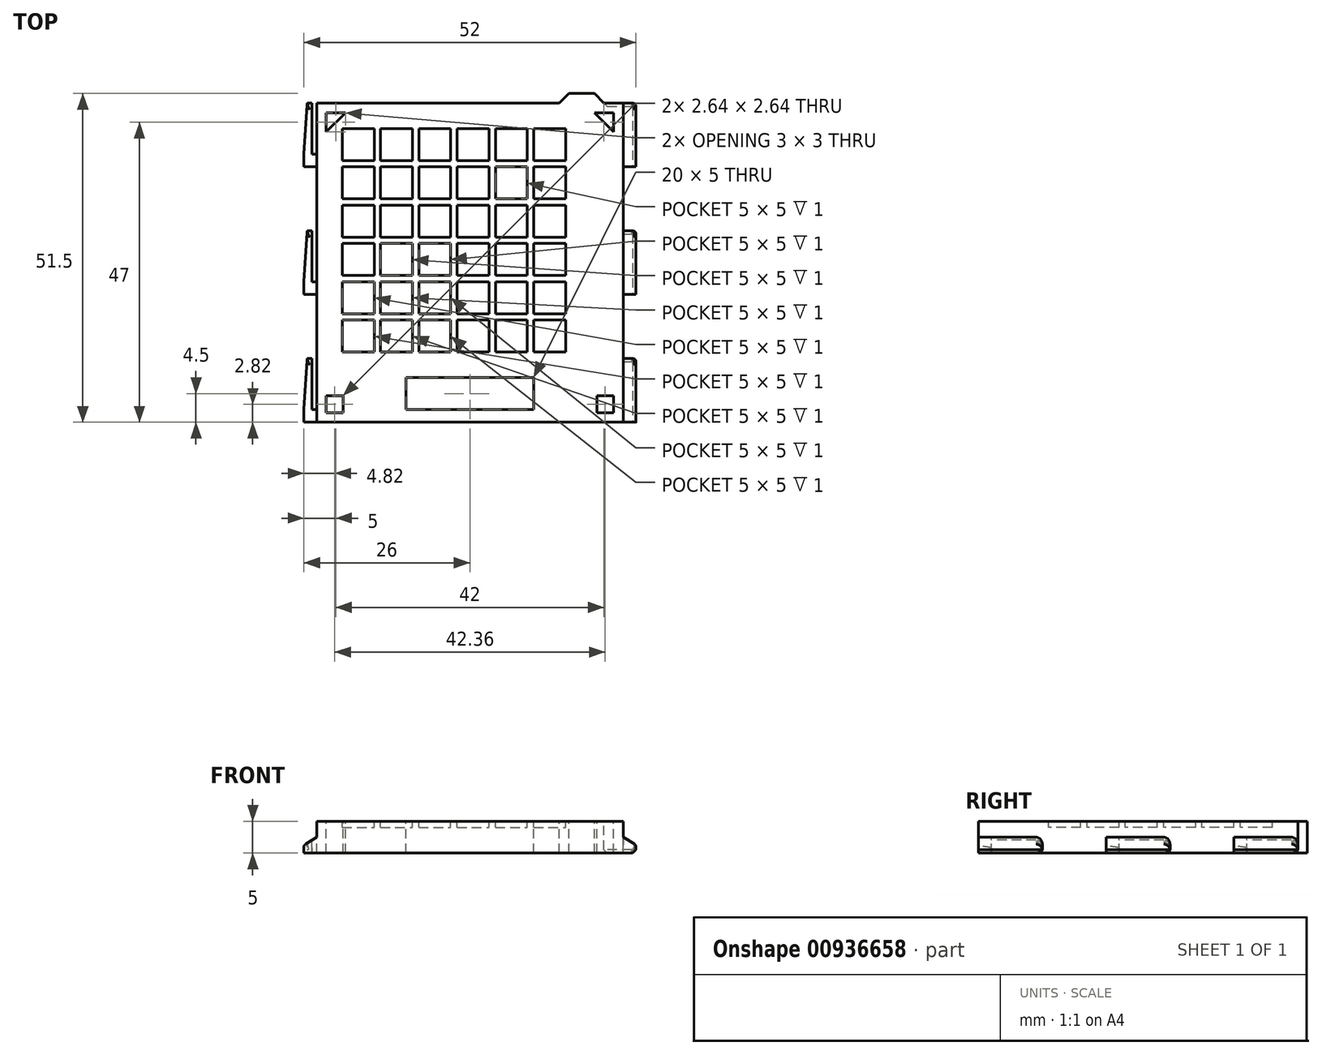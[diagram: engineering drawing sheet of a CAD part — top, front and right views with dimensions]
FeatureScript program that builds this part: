
annotation { "Feature Type Name" : "Feature", "Feature Type Description" : "" }
export const myFeature = defineFeature(function(context is Context, id is Id, definition is map)
    precondition{}
    {
        {
            var Q0;
            Q0=qCreatedBy(makeId("Top.planeOp"),FACE);
            var sketch = newSketch(context, id + "F0", { "sketchPlane" : qUnion([Q0])});
            skLineSegment(sketch, "E0.bottom", {"start": v(0, 0) * mm, "end": v(48, 0) * mm});
            skLineSegment(sketch, "E0.top", {"start": v(0, -50) * mm, "end": v(48, -50) * mm});
            skLineSegment(sketch, "E0.left", {"start": v(0, 0) * mm, "end": v(0, -50) * mm});
            skLineSegment(sketch, "E0.right", {"start": v(48, 0) * mm, "end": v(48, -50) * mm});
            skSolve(sketch);
        }
        {
            var Q0;
            Q0=makeQuery(id+"F0.imprint","IMPRINT",FACE,{"disambiguationData":[TD([[makeQuery(id+"F0.imprint","IMPRINT",EDGE,{"derivedFrom":sQuery(id+"F0.wireOp",EDGE,"E0.bottom")}),-1.0]])]});
            extrude(context, id + "F1", {"entities" : qUnion([Q0]), "depth" : 5 * mm, "offsetDistance" : 25 * mm});
        }
        {
            var Q0;
            Q0=makeQuery(id+"F1.opExtrude","CAP_FACE",FACE,{"disambiguationData":[OSD([sQuery(id+"F0.wireOp",EDGE,"E0.bottom"),sQuery(id+"F0.wireOp",EDGE,"E0.top"),sQuery(id+"F0.wireOp",EDGE,"E0.left"),sQuery(id+"F0.wireOp",EDGE,"E0.right")])],"isStart":false});
            var sketch = newSketch(context, id + "F2", { "sketchPlane" : qUnion([Q0])});
            skLineSegment(sketch, "E1.bottom", {"start": v(4, -4) * mm, "end": v(9, -4) * mm});
            skLineSegment(sketch, "E1.top", {"start": v(4, -9) * mm, "end": v(9, -9) * mm});
            skLineSegment(sketch, "E1.left", {"start": v(4, -4) * mm, "end": v(4, -9) * mm});
            skLineSegment(sketch, "E1.right", {"start": v(9, -4) * mm, "end": v(9, -9) * mm});
            skLineSegment(sketch, "E2.0.1.0", {"start": v(4, -15) * mm, "end": v(9, -15) * mm});
            skLineSegment(sketch, "E2.0.1.1", {"start": v(9, -10) * mm, "end": v(9, -15) * mm});
            skLineSegment(sketch, "E2.0.1.2", {"start": v(4, -10) * mm, "end": v(4, -15) * mm});
            skLineSegment(sketch, "E2.0.1.3", {"start": v(4, -10) * mm, "end": v(9, -10) * mm});
            skLineSegment(sketch, "E2.0.2.0", {"start": v(4, -21) * mm, "end": v(9, -21) * mm});
            skLineSegment(sketch, "E2.0.2.1", {"start": v(9, -16) * mm, "end": v(9, -21) * mm});
            skLineSegment(sketch, "E2.0.2.2", {"start": v(4, -16) * mm, "end": v(4, -21) * mm});
            skLineSegment(sketch, "E2.0.2.3", {"start": v(4, -16) * mm, "end": v(9, -16) * mm});
            skLineSegment(sketch, "E2.0.3.0", {"start": v(4, -27) * mm, "end": v(9, -27) * mm});
            skLineSegment(sketch, "E2.0.3.1", {"start": v(9, -22) * mm, "end": v(9, -27) * mm});
            skLineSegment(sketch, "E2.0.3.2", {"start": v(4, -22) * mm, "end": v(4, -27) * mm});
            skLineSegment(sketch, "E2.0.3.3", {"start": v(4, -22) * mm, "end": v(9, -22) * mm});
            skLineSegment(sketch, "E2.0.4.0", {"start": v(4, -33) * mm, "end": v(9, -33) * mm});
            skLineSegment(sketch, "E2.0.4.1", {"start": v(9, -28) * mm, "end": v(9, -33) * mm});
            skLineSegment(sketch, "E2.0.4.2", {"start": v(4, -28) * mm, "end": v(4, -33) * mm});
            skLineSegment(sketch, "E2.0.4.3", {"start": v(4, -28) * mm, "end": v(9, -28) * mm});
            skLineSegment(sketch, "E2.0.5.0", {"start": v(4, -39) * mm, "end": v(9, -39) * mm});
            skLineSegment(sketch, "E2.0.5.1", {"start": v(9, -34) * mm, "end": v(9, -39) * mm});
            skLineSegment(sketch, "E2.0.5.2", {"start": v(4, -34) * mm, "end": v(4, -39) * mm});
            skLineSegment(sketch, "E2.0.5.3", {"start": v(4, -34) * mm, "end": v(9, -34) * mm});
            skLineSegment(sketch, "E2.1.0.0", {"start": v(10, -9) * mm, "end": v(15, -9) * mm});
            skLineSegment(sketch, "E2.1.0.1", {"start": v(15, -4) * mm, "end": v(15, -9) * mm});
            skLineSegment(sketch, "E2.1.0.2", {"start": v(10, -4) * mm, "end": v(10, -9) * mm});
            skLineSegment(sketch, "E2.1.0.3", {"start": v(10, -4) * mm, "end": v(15, -4) * mm});
            skLineSegment(sketch, "E2.1.1.0", {"start": v(10, -15) * mm, "end": v(15, -15) * mm});
            skLineSegment(sketch, "E2.1.1.1", {"start": v(15, -10) * mm, "end": v(15, -15) * mm});
            skLineSegment(sketch, "E2.1.1.2", {"start": v(10, -10) * mm, "end": v(10, -15) * mm});
            skLineSegment(sketch, "E2.1.1.3", {"start": v(10, -10) * mm, "end": v(15, -10) * mm});
            skLineSegment(sketch, "E2.1.2.0", {"start": v(10, -21) * mm, "end": v(15, -21) * mm});
            skLineSegment(sketch, "E2.1.2.1", {"start": v(15, -16) * mm, "end": v(15, -21) * mm});
            skLineSegment(sketch, "E2.1.2.2", {"start": v(10, -16) * mm, "end": v(10, -21) * mm});
            skLineSegment(sketch, "E2.1.2.3", {"start": v(10, -16) * mm, "end": v(15, -16) * mm});
            skLineSegment(sketch, "E2.1.3.0", {"start": v(10, -27) * mm, "end": v(15, -27) * mm});
            skLineSegment(sketch, "E2.1.3.1", {"start": v(15, -22) * mm, "end": v(15, -27) * mm});
            skLineSegment(sketch, "E2.1.3.2", {"start": v(10, -22) * mm, "end": v(10, -27) * mm});
            skLineSegment(sketch, "E2.1.3.3", {"start": v(10, -22) * mm, "end": v(15, -22) * mm});
            skLineSegment(sketch, "E2.1.4.0", {"start": v(10, -33) * mm, "end": v(15, -33) * mm});
            skLineSegment(sketch, "E2.1.4.1", {"start": v(15, -28) * mm, "end": v(15, -33) * mm});
            skLineSegment(sketch, "E2.1.4.2", {"start": v(10, -28) * mm, "end": v(10, -33) * mm});
            skLineSegment(sketch, "E2.1.4.3", {"start": v(10, -28) * mm, "end": v(15, -28) * mm});
            skLineSegment(sketch, "E2.1.5.0", {"start": v(10, -39) * mm, "end": v(15, -39) * mm});
            skLineSegment(sketch, "E2.1.5.1", {"start": v(15, -34) * mm, "end": v(15, -39) * mm});
            skLineSegment(sketch, "E2.1.5.2", {"start": v(10, -34) * mm, "end": v(10, -39) * mm});
            skLineSegment(sketch, "E2.1.5.3", {"start": v(10, -34) * mm, "end": v(15, -34) * mm});
            skLineSegment(sketch, "E2.2.0.0", {"start": v(16, -9) * mm, "end": v(21, -9) * mm});
            skLineSegment(sketch, "E2.2.0.1", {"start": v(21, -4) * mm, "end": v(21, -9) * mm});
            skLineSegment(sketch, "E2.2.0.2", {"start": v(16, -4) * mm, "end": v(16, -9) * mm});
            skLineSegment(sketch, "E2.2.0.3", {"start": v(16, -4) * mm, "end": v(21, -4) * mm});
            skLineSegment(sketch, "E2.2.1.0", {"start": v(16, -15) * mm, "end": v(21, -15) * mm});
            skLineSegment(sketch, "E2.2.1.1", {"start": v(21, -10) * mm, "end": v(21, -15) * mm});
            skLineSegment(sketch, "E2.2.1.2", {"start": v(16, -10) * mm, "end": v(16, -15) * mm});
            skLineSegment(sketch, "E2.2.1.3", {"start": v(16, -10) * mm, "end": v(21, -10) * mm});
            skLineSegment(sketch, "E2.2.2.0", {"start": v(16, -21) * mm, "end": v(21, -21) * mm});
            skLineSegment(sketch, "E2.2.2.1", {"start": v(21, -16) * mm, "end": v(21, -21) * mm});
            skLineSegment(sketch, "E2.2.2.2", {"start": v(16, -16) * mm, "end": v(16, -21) * mm});
            skLineSegment(sketch, "E2.2.2.3", {"start": v(16, -16) * mm, "end": v(21, -16) * mm});
            skLineSegment(sketch, "E2.2.3.0", {"start": v(16, -27) * mm, "end": v(21, -27) * mm});
            skLineSegment(sketch, "E2.2.3.1", {"start": v(21, -22) * mm, "end": v(21, -27) * mm});
            skLineSegment(sketch, "E2.2.3.2", {"start": v(16, -22) * mm, "end": v(16, -27) * mm});
            skLineSegment(sketch, "E2.2.3.3", {"start": v(16, -22) * mm, "end": v(21, -22) * mm});
            skLineSegment(sketch, "E2.2.4.0", {"start": v(16, -33) * mm, "end": v(21, -33) * mm});
            skLineSegment(sketch, "E2.2.4.1", {"start": v(21, -28) * mm, "end": v(21, -33) * mm});
            skLineSegment(sketch, "E2.2.4.2", {"start": v(16, -28) * mm, "end": v(16, -33) * mm});
            skLineSegment(sketch, "E2.2.4.3", {"start": v(16, -28) * mm, "end": v(21, -28) * mm});
            skLineSegment(sketch, "E2.2.5.0", {"start": v(16, -39) * mm, "end": v(21, -39) * mm});
            skLineSegment(sketch, "E2.2.5.1", {"start": v(21, -34) * mm, "end": v(21, -39) * mm});
            skLineSegment(sketch, "E2.2.5.2", {"start": v(16, -34) * mm, "end": v(16, -39) * mm});
            skLineSegment(sketch, "E2.2.5.3", {"start": v(16, -34) * mm, "end": v(21, -34) * mm});
            skLineSegment(sketch, "E2.3.0.0", {"start": v(22, -9) * mm, "end": v(27, -9) * mm});
            skLineSegment(sketch, "E2.3.0.1", {"start": v(27, -4) * mm, "end": v(27, -9) * mm});
            skLineSegment(sketch, "E2.3.0.2", {"start": v(22, -4) * mm, "end": v(22, -9) * mm});
            skLineSegment(sketch, "E2.3.0.3", {"start": v(22, -4) * mm, "end": v(27, -4) * mm});
            skLineSegment(sketch, "E2.3.1.0", {"start": v(22, -15) * mm, "end": v(27, -15) * mm});
            skLineSegment(sketch, "E2.3.1.1", {"start": v(27, -10) * mm, "end": v(27, -15) * mm});
            skLineSegment(sketch, "E2.3.1.2", {"start": v(22, -10) * mm, "end": v(22, -15) * mm});
            skLineSegment(sketch, "E2.3.1.3", {"start": v(22, -10) * mm, "end": v(27, -10) * mm});
            skLineSegment(sketch, "E2.3.2.0", {"start": v(22, -21) * mm, "end": v(27, -21) * mm});
            skLineSegment(sketch, "E2.3.2.1", {"start": v(27, -16) * mm, "end": v(27, -21) * mm});
            skLineSegment(sketch, "E2.3.2.2", {"start": v(22, -16) * mm, "end": v(22, -21) * mm});
            skLineSegment(sketch, "E2.3.2.3", {"start": v(22, -16) * mm, "end": v(27, -16) * mm});
            skLineSegment(sketch, "E2.3.3.0", {"start": v(22, -27) * mm, "end": v(27, -27) * mm});
            skLineSegment(sketch, "E2.3.3.1", {"start": v(27, -22) * mm, "end": v(27, -27) * mm});
            skLineSegment(sketch, "E2.3.3.2", {"start": v(22, -22) * mm, "end": v(22, -27) * mm});
            skLineSegment(sketch, "E2.3.3.3", {"start": v(22, -22) * mm, "end": v(27, -22) * mm});
            skLineSegment(sketch, "E2.3.4.0", {"start": v(22, -33) * mm, "end": v(27, -33) * mm});
            skLineSegment(sketch, "E2.3.4.1", {"start": v(27, -28) * mm, "end": v(27, -33) * mm});
            skLineSegment(sketch, "E2.3.4.2", {"start": v(22, -28) * mm, "end": v(22, -33) * mm});
            skLineSegment(sketch, "E2.3.4.3", {"start": v(22, -28) * mm, "end": v(27, -28) * mm});
            skLineSegment(sketch, "E2.3.5.0", {"start": v(22, -39) * mm, "end": v(27, -39) * mm});
            skLineSegment(sketch, "E2.3.5.1", {"start": v(27, -34) * mm, "end": v(27, -39) * mm});
            skLineSegment(sketch, "E2.3.5.2", {"start": v(22, -34) * mm, "end": v(22, -39) * mm});
            skLineSegment(sketch, "E2.3.5.3", {"start": v(22, -34) * mm, "end": v(27, -34) * mm});
            skLineSegment(sketch, "E2.4.0.0", {"start": v(28, -9) * mm, "end": v(33, -9) * mm});
            skLineSegment(sketch, "E2.4.0.1", {"start": v(33, -4) * mm, "end": v(33, -9) * mm});
            skLineSegment(sketch, "E2.4.0.2", {"start": v(28, -4) * mm, "end": v(28, -9) * mm});
            skLineSegment(sketch, "E2.4.0.3", {"start": v(28, -4) * mm, "end": v(33, -4) * mm});
            skLineSegment(sketch, "E2.4.1.0", {"start": v(28, -15) * mm, "end": v(33, -15) * mm});
            skLineSegment(sketch, "E2.4.1.1", {"start": v(33, -10) * mm, "end": v(33, -15) * mm});
            skLineSegment(sketch, "E2.4.1.2", {"start": v(28, -10) * mm, "end": v(28, -15) * mm});
            skLineSegment(sketch, "E2.4.1.3", {"start": v(28, -10) * mm, "end": v(33, -10) * mm});
            skLineSegment(sketch, "E2.4.2.0", {"start": v(28, -21) * mm, "end": v(33, -21) * mm});
            skLineSegment(sketch, "E2.4.2.1", {"start": v(33, -16) * mm, "end": v(33, -21) * mm});
            skLineSegment(sketch, "E2.4.2.2", {"start": v(28, -16) * mm, "end": v(28, -21) * mm});
            skLineSegment(sketch, "E2.4.2.3", {"start": v(28, -16) * mm, "end": v(33, -16) * mm});
            skLineSegment(sketch, "E2.4.3.0", {"start": v(28, -27) * mm, "end": v(33, -27) * mm});
            skLineSegment(sketch, "E2.4.3.1", {"start": v(33, -22) * mm, "end": v(33, -27) * mm});
            skLineSegment(sketch, "E2.4.3.2", {"start": v(28, -22) * mm, "end": v(28, -27) * mm});
            skLineSegment(sketch, "E2.4.3.3", {"start": v(28, -22) * mm, "end": v(33, -22) * mm});
            skLineSegment(sketch, "E2.4.4.0", {"start": v(28, -33) * mm, "end": v(33, -33) * mm});
            skLineSegment(sketch, "E2.4.4.1", {"start": v(33, -28) * mm, "end": v(33, -33) * mm});
            skLineSegment(sketch, "E2.4.4.2", {"start": v(28, -28) * mm, "end": v(28, -33) * mm});
            skLineSegment(sketch, "E2.4.4.3", {"start": v(28, -28) * mm, "end": v(33, -28) * mm});
            skLineSegment(sketch, "E2.4.5.0", {"start": v(28, -39) * mm, "end": v(33, -39) * mm});
            skLineSegment(sketch, "E2.4.5.1", {"start": v(33, -34) * mm, "end": v(33, -39) * mm});
            skLineSegment(sketch, "E2.4.5.2", {"start": v(28, -34) * mm, "end": v(28, -39) * mm});
            skLineSegment(sketch, "E2.4.5.3", {"start": v(28, -34) * mm, "end": v(33, -34) * mm});
            skLineSegment(sketch, "E2.5.0.0", {"start": v(34, -9) * mm, "end": v(39, -9) * mm});
            skLineSegment(sketch, "E2.5.0.1", {"start": v(39, -4) * mm, "end": v(39, -9) * mm});
            skLineSegment(sketch, "E2.5.0.2", {"start": v(34, -4) * mm, "end": v(34, -9) * mm});
            skLineSegment(sketch, "E2.5.0.3", {"start": v(34, -4) * mm, "end": v(39, -4) * mm});
            skLineSegment(sketch, "E2.5.1.0", {"start": v(34, -15) * mm, "end": v(39, -15) * mm});
            skLineSegment(sketch, "E2.5.1.1", {"start": v(39, -10) * mm, "end": v(39, -15) * mm});
            skLineSegment(sketch, "E2.5.1.2", {"start": v(34, -10) * mm, "end": v(34, -15) * mm});
            skLineSegment(sketch, "E2.5.1.3", {"start": v(34, -10) * mm, "end": v(39, -10) * mm});
            skLineSegment(sketch, "E2.5.2.0", {"start": v(34, -21) * mm, "end": v(39, -21) * mm});
            skLineSegment(sketch, "E2.5.2.1", {"start": v(39, -16) * mm, "end": v(39, -21) * mm});
            skLineSegment(sketch, "E2.5.2.2", {"start": v(34, -16) * mm, "end": v(34, -21) * mm});
            skLineSegment(sketch, "E2.5.2.3", {"start": v(34, -16) * mm, "end": v(39, -16) * mm});
            skLineSegment(sketch, "E2.5.3.0", {"start": v(34, -27) * mm, "end": v(39, -27) * mm});
            skLineSegment(sketch, "E2.5.3.1", {"start": v(39, -22) * mm, "end": v(39, -27) * mm});
            skLineSegment(sketch, "E2.5.3.2", {"start": v(34, -22) * mm, "end": v(34, -27) * mm});
            skLineSegment(sketch, "E2.5.3.3", {"start": v(34, -22) * mm, "end": v(39, -22) * mm});
            skLineSegment(sketch, "E2.5.4.0", {"start": v(34, -33) * mm, "end": v(39, -33) * mm});
            skLineSegment(sketch, "E2.5.4.1", {"start": v(39, -28) * mm, "end": v(39, -33) * mm});
            skLineSegment(sketch, "E2.5.4.2", {"start": v(34, -28) * mm, "end": v(34, -33) * mm});
            skLineSegment(sketch, "E2.5.4.3", {"start": v(34, -28) * mm, "end": v(39, -28) * mm});
            skLineSegment(sketch, "E2.5.5.0", {"start": v(34, -39) * mm, "end": v(39, -39) * mm});
            skLineSegment(sketch, "E2.5.5.1", {"start": v(39, -34) * mm, "end": v(39, -39) * mm});
            skLineSegment(sketch, "E2.5.5.2", {"start": v(34, -34) * mm, "end": v(34, -39) * mm});
            skLineSegment(sketch, "E2.5.5.3", {"start": v(34, -34) * mm, "end": v(39, -34) * mm});
            skLineSegment(sketch, "E2.direction1", {"start": v(4, -9) * mm, "end": v(10, -9) * mm, "construction": true});
            skLineSegment(sketch, "E2.direction2", {"start": v(4, -9) * mm, "end": v(4, -15) * mm, "construction": true});
            skSolve(sketch);
        }
        {
            var Q0;
            Q0=makeQuery(id+"F2.imprint","IMPRINT",FACE,{"disambiguationData":[TD([[makeQuery(id+"F2.imprint","IMPRINT",EDGE,{"derivedFrom":sQuery(id+"F2.wireOp",EDGE,"E1.bottom")}),-1.0]])]});
            var Q1;
            Q1=makeQuery(id+"F2.imprint","IMPRINT",FACE,{"disambiguationData":[TD([[makeQuery(id+"F2.imprint","IMPRINT",EDGE,{"derivedFrom":sQuery(id+"F2.wireOp",EDGE,"E2.0.1.0")}),1.0]])]});
            var Q2;
            Q2=makeQuery(id+"F2.imprint","IMPRINT",FACE,{"disambiguationData":[TD([[makeQuery(id+"F2.imprint","IMPRINT",EDGE,{"derivedFrom":sQuery(id+"F2.wireOp",EDGE,"E2.0.2.0")}),1.0]])]});
            var Q3;
            Q3=makeQuery(id+"F2.imprint","IMPRINT",FACE,{"disambiguationData":[TD([[makeQuery(id+"F2.imprint","IMPRINT",EDGE,{"derivedFrom":sQuery(id+"F2.wireOp",EDGE,"E2.0.3.0")}),1.0]])]});
            var Q4;
            Q4=makeQuery(id+"F2.imprint","IMPRINT",FACE,{"disambiguationData":[TD([[makeQuery(id+"F2.imprint","IMPRINT",EDGE,{"derivedFrom":sQuery(id+"F2.wireOp",EDGE,"E2.2.0.0")}),1.0]])]});
            var Q5;
            Q5=makeQuery(id+"F2.imprint","IMPRINT",FACE,{"disambiguationData":[TD([[makeQuery(id+"F2.imprint","IMPRINT",EDGE,{"derivedFrom":sQuery(id+"F2.wireOp",EDGE,"E2.2.1.0")}),1.0]])]});
            var Q6;
            Q6=makeQuery(id+"F2.imprint","IMPRINT",FACE,{"disambiguationData":[TD([[makeQuery(id+"F2.imprint","IMPRINT",EDGE,{"derivedFrom":sQuery(id+"F2.wireOp",EDGE,"E2.2.2.0")}),1.0]])]});
            var Q7;
            Q7=makeQuery(id+"F2.imprint","IMPRINT",FACE,{"disambiguationData":[TD([[makeQuery(id+"F2.imprint","IMPRINT",EDGE,{"derivedFrom":sQuery(id+"F2.wireOp",EDGE,"E2.4.3.0")}),1.0]])]});
            var Q8;
            Q8=makeQuery(id+"F2.imprint","IMPRINT",FACE,{"disambiguationData":[TD([[makeQuery(id+"F2.imprint","IMPRINT",EDGE,{"derivedFrom":sQuery(id+"F2.wireOp",EDGE,"E2.4.4.0")}),1.0]])]});
            var Q9;
            Q9=makeQuery(id+"F2.imprint","IMPRINT",FACE,{"disambiguationData":[TD([[makeQuery(id+"F2.imprint","IMPRINT",EDGE,{"derivedFrom":sQuery(id+"F2.wireOp",EDGE,"E2.4.5.0")}),1.0]])]});
            var Q10;
            Q10=makeQuery(id+"F2.imprint","IMPRINT",FACE,{"disambiguationData":[TD([[makeQuery(id+"F2.imprint","IMPRINT",EDGE,{"derivedFrom":sQuery(id+"F2.wireOp",EDGE,"E2.5.0.0")}),1.0]])]});
            var Q11;
            Q11=makeQuery(id+"F2.imprint","IMPRINT",FACE,{"disambiguationData":[TD([[makeQuery(id+"F2.imprint","IMPRINT",EDGE,{"derivedFrom":sQuery(id+"F2.wireOp",EDGE,"E2.5.1.0")}),1.0]])]});
            var Q12;
            Q12=makeQuery(id+"F2.imprint","IMPRINT",FACE,{"disambiguationData":[TD([[makeQuery(id+"F2.imprint","IMPRINT",EDGE,{"derivedFrom":sQuery(id+"F2.wireOp",EDGE,"E2.5.2.0")}),1.0]])]});
            var Q13;
            Q13=makeQuery(id+"F2.imprint","IMPRINT",FACE,{"disambiguationData":[TD([[makeQuery(id+"F2.imprint","IMPRINT",EDGE,{"derivedFrom":sQuery(id+"F2.wireOp",EDGE,"E2.5.5.0")}),1.0]])]});
            var Q14;
            Q14=makeQuery(id+"F2.imprint","IMPRINT",FACE,{"disambiguationData":[TD([[makeQuery(id+"F2.imprint","IMPRINT",EDGE,{"derivedFrom":sQuery(id+"F2.wireOp",EDGE,"E2.5.4.0")}),1.0]])]});
            var Q15;
            Q15=makeQuery(id+"F2.imprint","IMPRINT",FACE,{"disambiguationData":[TD([[makeQuery(id+"F2.imprint","IMPRINT",EDGE,{"derivedFrom":sQuery(id+"F2.wireOp",EDGE,"E2.5.3.0")}),1.0]])]});
            var Q16;
            Q16=makeQuery(id+"F2.imprint","IMPRINT",FACE,{"disambiguationData":[TD([[makeQuery(id+"F2.imprint","IMPRINT",EDGE,{"derivedFrom":sQuery(id+"F2.wireOp",EDGE,"E2.4.2.0")}),1.0]])]});
            var Q17;
            Q17=makeQuery(id+"F2.imprint","IMPRINT",FACE,{"disambiguationData":[TD([[makeQuery(id+"F2.imprint","IMPRINT",EDGE,{"derivedFrom":sQuery(id+"F2.wireOp",EDGE,"E2.4.1.0")}),1.0]])]});
            var Q18;
            Q18=makeQuery(id+"F2.imprint","IMPRINT",FACE,{"disambiguationData":[TD([[makeQuery(id+"F2.imprint","IMPRINT",EDGE,{"derivedFrom":sQuery(id+"F2.wireOp",EDGE,"E2.4.0.0")}),1.0]])]});
            var Q19;
            Q19=makeQuery(id+"F2.imprint","IMPRINT",FACE,{"disambiguationData":[TD([[makeQuery(id+"F2.imprint","IMPRINT",EDGE,{"derivedFrom":sQuery(id+"F2.wireOp",EDGE,"E2.3.5.0")}),1.0]])]});
            var Q20;
            Q20=makeQuery(id+"F2.imprint","IMPRINT",FACE,{"disambiguationData":[TD([[makeQuery(id+"F2.imprint","IMPRINT",EDGE,{"derivedFrom":sQuery(id+"F2.wireOp",EDGE,"E2.3.4.0")}),1.0]])]});
            var Q21;
            Q21=makeQuery(id+"F2.imprint","IMPRINT",FACE,{"disambiguationData":[TD([[makeQuery(id+"F2.imprint","IMPRINT",EDGE,{"derivedFrom":sQuery(id+"F2.wireOp",EDGE,"E2.3.3.0")}),1.0]])]});
            var Q22;
            Q22=makeQuery(id+"F2.imprint","IMPRINT",FACE,{"disambiguationData":[TD([[makeQuery(id+"F2.imprint","IMPRINT",EDGE,{"derivedFrom":sQuery(id+"F2.wireOp",EDGE,"E2.3.2.0")}),1.0]])]});
            var Q23;
            Q23=makeQuery(id+"F2.imprint","IMPRINT",FACE,{"disambiguationData":[TD([[makeQuery(id+"F2.imprint","IMPRINT",EDGE,{"derivedFrom":sQuery(id+"F2.wireOp",EDGE,"E2.3.1.0")}),1.0]])]});
            var Q24;
            Q24=makeQuery(id+"F2.imprint","IMPRINT",FACE,{"disambiguationData":[TD([[makeQuery(id+"F2.imprint","IMPRINT",EDGE,{"derivedFrom":sQuery(id+"F2.wireOp",EDGE,"E2.3.0.0")}),1.0]])]});
            var Q25;
            Q25=makeQuery(id+"F2.imprint","IMPRINT",FACE,{"disambiguationData":[TD([[makeQuery(id+"F2.imprint","IMPRINT",EDGE,{"derivedFrom":sQuery(id+"F2.wireOp",EDGE,"E2.2.5.0")}),1.0]])]});
            var Q26;
            Q26=makeQuery(id+"F2.imprint","IMPRINT",FACE,{"disambiguationData":[TD([[makeQuery(id+"F2.imprint","IMPRINT",EDGE,{"derivedFrom":sQuery(id+"F2.wireOp",EDGE,"E2.2.4.0")}),1.0]])]});
            var Q27;
            Q27=makeQuery(id+"F2.imprint","IMPRINT",FACE,{"disambiguationData":[TD([[makeQuery(id+"F2.imprint","IMPRINT",EDGE,{"derivedFrom":sQuery(id+"F2.wireOp",EDGE,"E2.1.5.0")}),1.0]])]});
            var Q28;
            Q28=makeQuery(id+"F2.imprint","IMPRINT",FACE,{"disambiguationData":[TD([[makeQuery(id+"F2.imprint","IMPRINT",EDGE,{"derivedFrom":sQuery(id+"F2.wireOp",EDGE,"E2.0.5.0")}),1.0]])]});
            var Q29;
            Q29=makeQuery(id+"F2.imprint","IMPRINT",FACE,{"disambiguationData":[TD([[makeQuery(id+"F2.imprint","IMPRINT",EDGE,{"derivedFrom":sQuery(id+"F2.wireOp",EDGE,"E2.0.4.0")}),1.0]])]});
            var Q30;
            Q30=makeQuery(id+"F2.imprint","IMPRINT",FACE,{"disambiguationData":[TD([[makeQuery(id+"F2.imprint","IMPRINT",EDGE,{"derivedFrom":sQuery(id+"F2.wireOp",EDGE,"E2.1.4.0")}),1.0]])]});
            var Q31;
            Q31=makeQuery(id+"F2.imprint","IMPRINT",FACE,{"disambiguationData":[TD([[makeQuery(id+"F2.imprint","IMPRINT",EDGE,{"derivedFrom":sQuery(id+"F2.wireOp",EDGE,"E2.1.3.0")}),1.0]])]});
            var Q32;
            Q32=makeQuery(id+"F2.imprint","IMPRINT",FACE,{"disambiguationData":[TD([[makeQuery(id+"F2.imprint","IMPRINT",EDGE,{"derivedFrom":sQuery(id+"F2.wireOp",EDGE,"E2.2.3.0")}),1.0]])]});
            var Q33;
            Q33=makeQuery(id+"F2.imprint","IMPRINT",FACE,{"disambiguationData":[TD([[makeQuery(id+"F2.imprint","IMPRINT",EDGE,{"derivedFrom":sQuery(id+"F2.wireOp",EDGE,"E2.1.2.0")}),1.0]])]});
            var Q34;
            Q34=makeQuery(id+"F2.imprint","IMPRINT",FACE,{"disambiguationData":[TD([[makeQuery(id+"F2.imprint","IMPRINT",EDGE,{"derivedFrom":sQuery(id+"F2.wireOp",EDGE,"E2.1.1.0")}),1.0]])]});
            var Q35;
            Q35=makeQuery(id+"F2.imprint","IMPRINT",FACE,{"disambiguationData":[TD([[makeQuery(id+"F2.imprint","IMPRINT",EDGE,{"derivedFrom":sQuery(id+"F2.wireOp",EDGE,"E2.1.0.0")}),1.0]])]});
            extrude(context, id + "F3", {"entities" : qUnion([Q0, Q1, Q2, Q3, Q4, Q5, Q6, Q7, Q8, Q9, Q10, Q11, Q12, Q13, Q14, Q15, Q16, Q17, Q18, Q19, Q20, Q21, Q22, Q23, Q24, Q25, Q26, Q27, Q28, Q29, Q30, Q31, Q32, Q33, Q34, Q35]), "operationType" : NewBodyOperationType.REMOVE, "oppositeDirection" : true, "depth" : 1 * mm, "offsetDistance" : 25 * mm});
        }
        {
            var Q0;
            Q0=makeQuery(id+"F1.opExtrude","SWEPT_FACE",FACE,{"disambiguationData":[OSD([sQuery(id+"F0.wireOp",EDGE,"E0.top")])]});
            var sketch = newSketch(context, id + "F4", { "sketchPlane" : qUnion([Q0])});
            skLineSegment(sketch, "E3", {"start": v(0, 0) * mm, "end": v(-2, 0) * mm});
            skLineSegment(sketch, "E4", {"start": v(48, 0) * mm, "end": v(50, 0) * mm});
            skLineSegment(sketch, "E5", {"start": v(50, 0) * mm, "end": v(50, 1.25) * mm});
            skLineSegment(sketch, "E6", {"start": v(50, 1.25) * mm, "end": v(48, 2.5) * mm});
            skLineSegment(sketch, "E7", {"start": v(-2, 0) * mm, "end": v(-2, 1.25) * mm});
            skLineSegment(sketch, "E8", {"start": v(-2, 1.25) * mm, "end": v(0, 2.5) * mm});
            skSolve(sketch);
        }
        {
            var Q0;
            {var subQ6=sQuery(id+"F4.wireOp",EDGE,"E3");Q0=makeQuery(id+"F4.imprint","IMPRINT",FACE,{"disambiguationData":[TD([[makeQuery(id+"F4.imprint","IMPRINT",EDGE,{"derivedFrom":subQ6}),-1.0]])]});}
            var Q1;
            {var subQ1=sQuery(id+"F4.wireOp",EDGE,"E4");Q1=makeQuery(id+"F4.imprint","IMPRINT",FACE,{"disambiguationData":[TD([[makeQuery(id+"F4.imprint","IMPRINT",EDGE,{"derivedFrom":subQ1}),1.0]])]});}
            var Q2;
            Q2=makeQuery(id+"F1.opExtrude","SWEPT_FACE",FACE,{"disambiguationData":[OSD([sQuery(id+"F0.wireOp",EDGE,"E0.bottom")])]});
            extrude(context, id + "F5", {"entities" : qUnion([Q0, Q1]), "operationType" : NewBodyOperationType.ADD, "endBound" : BoundingType.UP_TO_SURFACE, "oppositeDirection" : true, "depth" : 25 * mm, "endBoundEntityFace" : qUnion([Q2]), "offsetDistance" : 25 * mm});
        }
        {
            var Q0;
            Q0=makeQuery(id+"F1.opExtrude","CAP_FACE",FACE,{"disambiguationData":[OSD([sQuery(id+"F0.wireOp",EDGE,"E0.bottom"),sQuery(id+"F0.wireOp",EDGE,"E0.top"),sQuery(id+"F0.wireOp",EDGE,"E0.left"),sQuery(id+"F0.wireOp",EDGE,"E0.right")])],"isStart":false});
            var sketch = newSketch(context, id + "F6", { "sketchPlane" : qUnion([Q0])});
            skPoint(sketch, "E9.firstSnap0", {"position": v(18.5, -4) * mm});
            skLineSegment(sketch, "E9.bottom", {"start": v(0, -10) * mm, "end": v(-6.52, -10) * mm});
            skLineSegment(sketch, "E9.top", {"start": v(0, -20) * mm, "end": v(-6.52, -20) * mm});
            skLineSegment(sketch, "E9.left", {"start": v(0, -10) * mm, "end": v(0, -20) * mm});
            skLineSegment(sketch, "E9.right", {"start": v(-6.52, -10) * mm, "end": v(-6.52, -20) * mm});
            skLineSegment(sketch, "E10", {"start": v(24, 0) * mm, "end": v(24, 8.51) * mm, "construction": true});
            skLineSegment(sketch, "E11.MirrorCS", {"start": v(48, -10) * mm, "end": v(54.52, -10) * mm});
            skLineSegment(sketch, "E12.MirrorCS", {"start": v(48, -10) * mm, "end": v(48, -20) * mm});
            skLineSegment(sketch, "E13.MirrorCS", {"start": v(48, -20) * mm, "end": v(54.52, -20) * mm});
            skLineSegment(sketch, "E14.MirrorCS", {"start": v(54.52, -10) * mm, "end": v(54.52, -20) * mm});
            skLineSegment(sketch, "E15.0.1.0", {"start": v(-6.52, -30) * mm, "end": v(-6.52, -40) * mm});
            skLineSegment(sketch, "E15.0.1.1", {"start": v(0, -30) * mm, "end": v(-6.52, -30) * mm});
            skLineSegment(sketch, "E15.0.1.2", {"start": v(0, -40) * mm, "end": v(-6.52, -40) * mm});
            skLineSegment(sketch, "E15.0.1.3", {"start": v(0, -30) * mm, "end": v(0, -40) * mm});
            skLineSegment(sketch, "E15.0.1.4", {"start": v(48, -30) * mm, "end": v(54.52, -30) * mm});
            skLineSegment(sketch, "E15.0.1.5", {"start": v(48, -30) * mm, "end": v(48, -40) * mm});
            skLineSegment(sketch, "E15.0.1.6", {"start": v(54.52, -30) * mm, "end": v(54.52, -40) * mm});
            skLineSegment(sketch, "E15.0.1.7", {"start": v(48, -40) * mm, "end": v(54.52, -40) * mm});
            skLineSegment(sketch, "E15.direction1", {"start": v(-6.52, -20) * mm, "end": v(18.48, -20) * mm, "construction": true});
            skLineSegment(sketch, "E15.direction2", {"start": v(-6.52, -20) * mm, "end": v(-6.52, -40) * mm, "construction": true});
            skSolve(sketch);
        }
        {
            var Q0;
            Q0=makeQuery(id+"F6.imprint","IMPRINT",FACE,{"disambiguationData":[TD([[makeQuery(id+"F6.imprint","IMPRINT",EDGE,{"derivedFrom":sQuery(id+"F6.wireOp",EDGE,"E9.bottom")}),1.0]])]});
            var Q1;
            Q1=makeQuery(id+"F6.imprint","IMPRINT",FACE,{"disambiguationData":[TD([[makeQuery(id+"F6.imprint","IMPRINT",EDGE,{"derivedFrom":sQuery(id+"F6.wireOp",EDGE,"E15.0.1.0")}),1.0]])]});
            var Q2;
            Q2=makeQuery(id+"F6.imprint","IMPRINT",FACE,{"disambiguationData":[TD([[makeQuery(id+"F6.imprint","IMPRINT",EDGE,{"derivedFrom":sQuery(id+"F6.wireOp",EDGE,"E15.0.1.4")}),-1.0]])]});
            var Q3;
            Q3=makeQuery(id+"F6.imprint","IMPRINT",FACE,{"disambiguationData":[TD([[makeQuery(id+"F6.imprint","IMPRINT",EDGE,{"derivedFrom":sQuery(id+"F6.wireOp",EDGE,"E11.MirrorCS")}),-1.0]])]});
            extrude(context, id + "F7", {"entities" : qUnion([Q0, Q1, Q2, Q3]), "operationType" : NewBodyOperationType.REMOVE, "oppositeDirection" : true, "depth" : 25 * mm, "offsetDistance" : 25 * mm});
        }
        {
            var Q0;
            Q0=makeQuery(id+"F1.opExtrude","CAP_FACE",FACE,{"disambiguationData":[OSD([sQuery(id+"F0.wireOp",EDGE,"E0.bottom"),sQuery(id+"F0.wireOp",EDGE,"E0.top"),sQuery(id+"F0.wireOp",EDGE,"E0.left"),sQuery(id+"F0.wireOp",EDGE,"E0.right")])],"isStart":false});
            var sketch = newSketch(context, id + "F8", { "sketchPlane" : qUnion([Q0])});
            skLineSegment(sketch, "E16", {"start": v(0, -48) * mm, "end": v(-0.75, -48) * mm});
            skLineSegment(sketch, "E17", {"start": v(-0.75, -48) * mm, "end": v(-0.75, -39.37) * mm});
            skLineSegment(sketch, "E18", {"start": v(-0.75, -39.37) * mm, "end": v(0, -39.37) * mm});
            skLineSegment(sketch, "E19", {"start": v(0, -39.37) * mm, "end": v(0, -48) * mm});
            skLineSegment(sketch, "E20.0.0", {"start": v(0, -40) * mm, "end": v(-1.31, -40) * mm});
            skLineSegment(sketch, "E20.0.1", {"start": v(-2, -40) * mm, "end": v(-2, -50) * mm});
            skLineSegment(sketch, "E20.0.2", {"start": v(-2, -50) * mm, "end": v(0, -50) * mm});
            skLineSegment(sketch, "E20.0.3", {"start": v(0, -50) * mm, "end": v(0, -40) * mm});
            skLineSegment(sketch, "E21", {"start": v(-2, -40) * mm, "end": v(-2, -47.93) * mm});
            skLineSegment(sketch, "E22", {"start": v(-2, -47.93) * mm, "end": v(-1.51, -40.19) * mm});
            skLineSegment(sketch, "E23", {"start": v(-1.5, -40) * mm, "end": v(-2, -40) * mm});
            skPoint(sketch, "E24.newPointA", {"position": v(-1.5, -40) * mm});
            skPoint(sketch, "E24.newPointB", {"position": v(-2, -40) * mm});
            skArc(sketch, "E24.filletArc", {"start": v(-1.31, -40) * mm, "mid": v(-1.45, -40.05) * mm, "end": v(-1.51, -40.19) * mm});
            skLineSegment(sketch, "E25", {"start": v(-1.31, -40) * mm, "end": v(-1.5, -40) * mm});
            skLineSegment(sketch, "E26.0.1.0", {"start": v(0, -28) * mm, "end": v(-0.75, -28) * mm});
            skLineSegment(sketch, "E26.0.1.1", {"start": v(-0.75, -28) * mm, "end": v(-0.75, -19.37) * mm});
            skLineSegment(sketch, "E26.0.1.2", {"start": v(-0.75, -19.37) * mm, "end": v(0, -19.37) * mm});
            skLineSegment(sketch, "E26.0.1.3", {"start": v(0, -19.37) * mm, "end": v(0, -28) * mm});
            skLineSegment(sketch, "E26.0.1.4", {"start": v(-2, -27.93) * mm, "end": v(-1.51, -20.19) * mm});
            skLineSegment(sketch, "E26.0.1.5", {"start": v(-2, -20) * mm, "end": v(-2, -30) * mm});
            skLineSegment(sketch, "E26.0.1.6", {"start": v(-1.5, -20) * mm, "end": v(-2, -20) * mm});
            skLineSegment(sketch, "E26.0.1.7", {"start": v(-1.31, -20) * mm, "end": v(-1.5, -20) * mm});
            skArc(sketch, "E26.0.1.8", {"start": v(-1.31, -20) * mm, "mid": v(-1.45, -20.05) * mm, "end": v(-1.51, -20.19) * mm});
            skLineSegment(sketch, "E26.0.2.0", {"start": v(0, -8) * mm, "end": v(-0.75, -8) * mm});
            skLineSegment(sketch, "E26.0.2.1", {"start": v(-0.75, -8) * mm, "end": v(-0.75, 0.63) * mm});
            skLineSegment(sketch, "E26.0.2.2", {"start": v(-0.75, 0.63) * mm, "end": v(0, 0.63) * mm});
            skLineSegment(sketch, "E26.0.2.3", {"start": v(0, 0.63) * mm, "end": v(0, -8) * mm});
            skLineSegment(sketch, "E26.0.2.4", {"start": v(-2, -7.93) * mm, "end": v(-1.51, -0.19) * mm});
            skLineSegment(sketch, "E26.0.2.5", {"start": v(-2, 0) * mm, "end": v(-2, -10) * mm});
            skLineSegment(sketch, "E26.0.2.6", {"start": v(-1.5, 0) * mm, "end": v(-2, 0) * mm});
            skLineSegment(sketch, "E26.0.2.7", {"start": v(-1.31, 0) * mm, "end": v(-1.5, 0) * mm});
            skArc(sketch, "E26.0.2.8", {"start": v(-1.31, 0) * mm, "mid": v(-1.45, -0.05) * mm, "end": v(-1.51, -0.19) * mm});
            skLineSegment(sketch, "E26.direction1", {"start": v(-0.75, -48) * mm, "end": v(24.25, -48) * mm, "construction": true});
            skLineSegment(sketch, "E26.direction2", {"start": v(-0.75, -48) * mm, "end": v(-0.75, -28) * mm, "construction": true});
            skLineSegment(sketch, "E27", {"start": v(24, 0.28) * mm, "end": v(24, 4.26) * mm, "construction": true});
            skPoint(sketch, "E27.startSnap0", {"position": v(24, 0) * mm});
            skSolve(sketch);
        }
        {
            var Q0;
            {var subQ0=sQuery(id+"F8.wireOp",EDGE,"E16");Q0=makeQuery(id+"F8.imprint","IMPRINT",FACE,{"disambiguationData":[TD([[makeQuery(id+"F8.imprint","IMPRINT",EDGE,{"derivedFrom":subQ0}),-1.0]])]});}
            var Q1;
            {var subQ0=sQuery(id+"F8.wireOp",EDGE,"E22");Q1=makeQuery(id+"F8.imprint","IMPRINT",FACE,{"disambiguationData":[TD([[makeQuery(id+"F8.imprint","IMPRINT",EDGE,{"derivedFrom":subQ0}),1.0]])]});}
            var Q2;
            Q2=makeQuery(id+"F8.imprint","IMPRINT",FACE,{"disambiguationData":[TD([[makeQuery(id+"F8.imprint","IMPRINT",EDGE,{"derivedFrom":sQuery(id+"F8.wireOp",EDGE,"E26.0.1.0")}),-1.0]])]});
            var Q3;
            {var subQ2=sQuery(id+"F8.wireOp",EDGE,"E26.0.1.4");Q3=makeQuery(id+"F8.imprint","IMPRINT",FACE,{"disambiguationData":[TD([[makeQuery(id+"F8.imprint","IMPRINT",EDGE,{"derivedFrom":subQ2}),1.0]])]});}
            var Q4;
            {var subQ2=sQuery(id+"F8.wireOp",EDGE,"E26.0.2.0");Q4=makeQuery(id+"F8.imprint","IMPRINT",FACE,{"disambiguationData":[TD([[makeQuery(id+"F8.imprint","IMPRINT",EDGE,{"derivedFrom":subQ2}),-1.0]])]});}
            var Q5;
            {var subQ2=sQuery(id+"F8.wireOp",EDGE,"E26.0.2.4");Q5=makeQuery(id+"F8.imprint","IMPRINT",FACE,{"disambiguationData":[TD([[makeQuery(id+"F8.imprint","IMPRINT",EDGE,{"derivedFrom":subQ2}),1.0]])]});}
            var Q6;
            Q6=makeQuery(id+"F8.imprint","IMPRINT",FACE,{"disambiguationData":[TD([[makeQuery(id+"F8.imprint","IMPRINT",EDGE,{"derivedFrom":sQuery(id+"F8.wireOp",EDGE,"e722379a-86f4-49ad-8a47-400355817b230.MirrorCS")}),1.0]])]});
            var Q7;
            Q7=makeQuery(id+"F8.imprint","IMPRINT",FACE,{"disambiguationData":[TD([[makeQuery(id+"F8.imprint","IMPRINT",EDGE,{"derivedFrom":sQuery(id+"F8.wireOp",EDGE,"d30c6836-2050-4577-9a9b-d798b92a200c0.MirrorCS")}),1.0]])]});
            var Q8;
            {var subQ2=sQuery(id+"F8.wireOp",EDGE,"4f4df0a9-7241-4b6c-b748-03f40ba930e40.MirrorCS");Q8=makeQuery(id+"F8.imprint","IMPRINT",FACE,{"disambiguationData":[TD([[makeQuery(id+"F8.imprint","IMPRINT",EDGE,{"derivedFrom":subQ2}),-1.0]])]});}
            var Q9;
            {var subQ1=sQuery(id+"F8.wireOp",EDGE,"5faf99e5-6c72-46fc-adc3-d1651bd9a6770.MirrorCS");Q9=makeQuery(id+"F8.imprint","IMPRINT",FACE,{"disambiguationData":[TD([[makeQuery(id+"F8.imprint","IMPRINT",EDGE,{"derivedFrom":subQ1}),-1.0]])]});}
            var Q10;
            Q10=makeQuery(id+"F8.imprint","IMPRINT",FACE,{"disambiguationData":[TD([[makeQuery(id+"F8.imprint","IMPRINT",EDGE,{"derivedFrom":sQuery(id+"F8.wireOp",EDGE,"cc6e77a2-de85-4070-afac-088a45ef221d0.MirrorCS")}),1.0]])]});
            var Q11;
            Q11=makeQuery(id+"F8.imprint","IMPRINT",FACE,{"disambiguationData":[TD([[makeQuery(id+"F8.imprint","IMPRINT",EDGE,{"derivedFrom":sQuery(id+"F8.wireOp",EDGE,"fa48c959-6260-4dcb-aed2-700d904f25cb0.MirrorCS")}),1.0]])]});
            extrude(context, id + "F9", {"entities" : qUnion([Q0, Q1, Q2, Q3, Q4, Q5, Q6, Q7, Q8, Q9, Q10, Q11]), "operationType" : NewBodyOperationType.REMOVE, "oppositeDirection" : true, "depth" : 25 * mm, "offsetDistance" : 25 * mm});
        }
        {
            var Q0;
            Q0=makeQuery(id+"F7.boolean.opBoolean","INTERSECT",EDGE,{"derivedFrom":[makeQuery(id+"F5.opExtrude","SWEPT_FACE",FACE,{"disambiguationData":[OSD([sQuery(id+"F4.wireOp",EDGE,"E8")])]}),makeQuery(id+"F7.opExtrude","SWEPT_FACE",FACE,{"disambiguationData":[OSD([sQuery(id+"F6.wireOp",EDGE,"E15.0.1.2")])]})]});
            var Q1;
            Q1=makeQuery(id+"F7.boolean.opBoolean","INTERSECT",EDGE,{"derivedFrom":[makeQuery(id+"F5.opExtrude","SWEPT_FACE",FACE,{"disambiguationData":[OSD([sQuery(id+"F4.wireOp",EDGE,"E8")])]}),makeQuery(id+"F7.opExtrude","SWEPT_FACE",FACE,{"disambiguationData":[OSD([sQuery(id+"F6.wireOp",EDGE,"E9.top")])]})]});
            var Q2;
            Q2=makeQuery(id+"F5.opExtrude","CAP_EDGE",EDGE,{"disambiguationData":[OSD([sQuery(id+"F4.wireOp",EDGE,"E8")])],"isStart":false});
            var Q3;
            Q3=makeQuery(id+"F5.opExtrude","CAP_EDGE",EDGE,{"disambiguationData":[OSD([sQuery(id+"F4.wireOp",EDGE,"E6")])],"isStart":false});
            var Q4;
            Q4=makeQuery(id+"F7.boolean.opBoolean","INTERSECT",EDGE,{"derivedFrom":[makeQuery(id+"F5.opExtrude","SWEPT_FACE",FACE,{"disambiguationData":[OSD([sQuery(id+"F4.wireOp",EDGE,"E6")])]}),makeQuery(id+"F7.opExtrude","SWEPT_FACE",FACE,{"disambiguationData":[OSD([sQuery(id+"F6.wireOp",EDGE,"E13.MirrorCS")])]})]});
            var Q5;
            Q5=makeQuery(id+"F7.boolean.opBoolean","INTERSECT",EDGE,{"derivedFrom":[makeQuery(id+"F5.opExtrude","SWEPT_FACE",FACE,{"disambiguationData":[OSD([sQuery(id+"F4.wireOp",EDGE,"E6")])]}),makeQuery(id+"F7.opExtrude","SWEPT_FACE",FACE,{"disambiguationData":[OSD([sQuery(id+"F6.wireOp",EDGE,"E15.0.1.7")])]})]});
            fillet(context, id + "F10", {"entities" : qUnion([Q0, Q1, Q2, Q3, Q4, Q5]), "radius" : 1 * mm, "tangentPropagation" : true, "allowEdgeOverflow" : false});
        }
        {
            var Q0;
            Q0=makeQuery(id+"F1.opExtrude","CAP_FACE",FACE,{"disambiguationData":[OSD([sQuery(id+"F0.wireOp",EDGE,"E0.bottom"),sQuery(id+"F0.wireOp",EDGE,"E0.top"),sQuery(id+"F0.wireOp",EDGE,"E0.left"),sQuery(id+"F0.wireOp",EDGE,"E0.right")])],"isStart":false});
            var sketch = newSketch(context, id + "F11", { "sketchPlane" : qUnion([Q0])});
            skLineSegment(sketch, "E28.bottom", {"start": v(14, -43) * mm, "end": v(34, -43) * mm});
            skLineSegment(sketch, "E28.top", {"start": v(14, -48) * mm, "end": v(34, -48) * mm});
            skLineSegment(sketch, "E28.left", {"start": v(14, -43) * mm, "end": v(14, -48) * mm});
            skLineSegment(sketch, "E28.right", {"start": v(34, -43) * mm, "end": v(34, -48) * mm});
            skLineSegment(sketch, "E29", {"start": v(24, -50) * mm, "end": v(24, -40.68) * mm, "construction": true});
            skPoint(sketch, "E30", {"position": v(24, -48) * mm});
            skLineSegment(sketch, "E31", {"start": v(1.5, -1.5) * mm, "end": v(1.5, -4.5) * mm});
            skLineSegment(sketch, "E32", {"start": v(1.5, -4.5) * mm, "end": v(4.5, -1.5) * mm});
            skLineSegment(sketch, "E33", {"start": v(4.5, -1.5) * mm, "end": v(1.5, -1.5) * mm});
            skLineSegment(sketch, "E34", {"start": v(24, 0) * mm, "end": v(24, -11.18) * mm, "construction": true});
            skLineSegment(sketch, "E35.MirrorCS", {"start": v(46.5, -4.5) * mm, "end": v(43.5, -1.5) * mm});
            skLineSegment(sketch, "E36.MirrorCS", {"start": v(46.5, -1.5) * mm, "end": v(46.5, -4.5) * mm});
            skLineSegment(sketch, "E37.MirrorCS", {"start": v(43.5, -1.5) * mm, "end": v(46.5, -1.5) * mm});
            skLineSegment(sketch, "E38", {"start": v(0, -25) * mm, "end": v(9, -25) * mm, "construction": true});
            skLineSegment(sketch, "E39.MirrorCS", {"start": v(1.5, -45.5) * mm, "end": v(4.5, -48.5) * mm});
            skLineSegment(sketch, "E40.MirrorCS", {"start": v(46.5, -45.5) * mm, "end": v(43.5, -48.5) * mm});
            skLineSegment(sketch, "E41.MirrorCS", {"start": v(43.5, -48.5) * mm, "end": v(46.5, -48.5) * mm});
            skLineSegment(sketch, "E42.MirrorCS", {"start": v(46.5, -48.5) * mm, "end": v(46.5, -45.5) * mm});
            skLineSegment(sketch, "E43.MirrorCS", {"start": v(4.5, -48.5) * mm, "end": v(1.5, -48.5) * mm});
            skLineSegment(sketch, "E44.MirrorCS", {"start": v(1.5, -48.5) * mm, "end": v(1.5, -45.5) * mm});
            skLineSegment(sketch, "E45", {"start": v(1.5, -45.5) * mm, "end": v(4.5, -45.5) * mm});
            skLineSegment(sketch, "E46", {"start": v(4.5, -45.5) * mm, "end": v(4.5, -48.5) * mm});
            skLineSegment(sketch, "E47", {"start": v(46.5, -45.5) * mm, "end": v(43.5, -45.5) * mm});
            skLineSegment(sketch, "E48", {"start": v(43.5, -45.5) * mm, "end": v(43.5, -48.5) * mm});
            skLineSegment(sketch, "E49", {"start": v(1.5, -45.86) * mm, "end": v(4.5, -45.86) * mm});
            skLineSegment(sketch, "E50", {"start": v(4.14, -45.5) * mm, "end": v(4.14, -48.5) * mm});
            skLineSegment(sketch, "E51", {"start": v(43.86, -48.5) * mm, "end": v(43.86, -45.5) * mm});
            skLineSegment(sketch, "E52", {"start": v(43.5, -45.86) * mm, "end": v(46.5, -45.86) * mm});
            skSolve(sketch);
        }
        {
            var Q0;
            Q0=makeQuery(id+"F11.imprint","IMPRINT",FACE,{"disambiguationData":[TD([[makeQuery(id+"F11.imprint","IMPRINT",EDGE,{"derivedFrom":sQuery(id+"F11.wireOp",EDGE,"E28.bottom")}),-1.0]])]});
            var Q1;
            Q1=makeQuery(id+"F11.imprint","IMPRINT",FACE,{"disambiguationData":[TD([[makeQuery(id+"F11.imprint","IMPRINT",EDGE,{"derivedFrom":sQuery(id+"F11.wireOp",EDGE,"E35.MirrorCS")}),-1.0]])]});
            var Q2;
            Q2=makeQuery(id+"F11.imprint","IMPRINT",FACE,{"disambiguationData":[TD([[makeQuery(id+"F11.imprint","IMPRINT",EDGE,{"derivedFrom":sQuery(id+"F11.wireOp",EDGE,"E31")}),1.0]])]});
            var Q3;
            Q3=makeQuery(id+"F11.imprint","IMPRINT",FACE,{"disambiguationData":[TD([[makeQuery(id+"F11.imprint","IMPRINT",EDGE,{"derivedFrom":sQuery(id+"F11.wireOp",EDGE,"E39.MirrorCS")}),1.0]])]});
            var Q4;
            Q4=makeQuery(id+"F11.imprint","IMPRINT",FACE,{"disambiguationData":[TD([[makeQuery(id+"F11.imprint","IMPRINT",EDGE,{"derivedFrom":sQuery(id+"F11.wireOp",EDGE,"E40.MirrorCS")}),-1.0]])]});
            var Q5;
            {var subQ3=sQuery(id+"F11.wireOp",EDGE,"E40.MirrorCS");var subQ7=sQuery(id+"F11.wireOp",EDGE,"E52");var subQ9=makeQuery(id+"F11.imprint","INTERSECT",VERTEX,{"derivedFrom":[subQ3,subQ7]});Q5=makeQuery(id+"F11.imprint","IMPRINT",FACE,{"disambiguationData":[TD([[makeQuery(id+"F11.imprint","IMPRINT",EDGE,{"disambiguationData":[TD([[subQ9,-1.0]])],"derivedFrom":subQ3}),1.0]])]});}
            var Q6;
            {var subQ0=sQuery(id+"F11.wireOp",EDGE,"E49");var subQ3=sQuery(id+"F11.wireOp",EDGE,"E39.MirrorCS");var subQ4=makeQuery(id+"F11.imprint","INTERSECT",VERTEX,{"derivedFrom":[subQ3,subQ0]});Q6=makeQuery(id+"F11.imprint","IMPRINT",FACE,{"disambiguationData":[TD([[makeQuery(id+"F11.imprint","IMPRINT",EDGE,{"disambiguationData":[TD([[subQ4,-1.0]])],"derivedFrom":subQ3}),-1.0]])]});}
            extrude(context, id + "F12", {"entities" : qUnion([Q0, Q1, Q2, Q3, Q4, Q5, Q6]), "operationType" : NewBodyOperationType.REMOVE, "oppositeDirection" : true, "depth" : 5 * mm, "offsetDistance" : 25 * mm});
        }
        {
            var Q0;
            {var subQ0=sQuery(id+"F4.wireOp",EDGE,"E6");var subQ1=sQuery(id+"F4.wireOp",EDGE,"E5");var subQ2=sQuery(id+"F0.wireOp",EDGE,"E0.top");Q0=makeQuery(id+"F7.boolean.opBoolean","SPLIT",EDGE,{"disambiguationData":[TD([makeQuery(id+"F1.opExtrude","SWEPT_FACE",FACE,{"disambiguationData":[OSD([subQ2])]})])],"derivedFrom":makeQuery(id+"F5.opExtrude","SWEPT_EDGE",EDGE,{"disambiguationData":[OSD([subQ1,subQ0])]})});}
            var Q1;
            {var subQ0=sQuery(id+"F4.wireOp",EDGE,"E5");var subQ1=sQuery(id+"F4.wireOp",EDGE,"E6");Q1=makeQuery(id+"F7.boolean.opBoolean","SPLIT",EDGE,{"disambiguationData":[TD([makeQuery(id+"F7.opExtrude","SWEPT_FACE",FACE,{"disambiguationData":[OSD([sQuery(id+"F6.wireOp",EDGE,"E13.MirrorCS")])]})])],"derivedFrom":makeQuery(id+"F5.opExtrude","SWEPT_EDGE",EDGE,{"disambiguationData":[OSD([subQ0,subQ1])]})});}
            var Q2;
            {var subQ0=sQuery(id+"F4.wireOp",EDGE,"E5");var subQ1=sQuery(id+"F4.wireOp",EDGE,"E6");Q2=makeQuery(id+"F7.boolean.opBoolean","SPLIT",EDGE,{"disambiguationData":[TD([makeQuery(id+"F1.opExtrude","SWEPT_FACE",FACE,{"disambiguationData":[OSD([sQuery(id+"F0.wireOp",EDGE,"E0.bottom")])]})])],"derivedFrom":makeQuery(id+"F5.opExtrude","SWEPT_EDGE",EDGE,{"disambiguationData":[OSD([subQ0,subQ1])]})});}
            fillet(context, id + "F13", {"entities" : qUnion([Q0, Q1, Q2]), "radius" : 0.5 * mm, "tangentPropagation" : true, "allowEdgeOverflow" : false});
        }
        {
            var Q0;
            Q0=makeQuery(id+"F1.opExtrude","CAP_FACE",FACE,{"disambiguationData":[OSD([sQuery(id+"F0.wireOp",EDGE,"E0.bottom"),sQuery(id+"F0.wireOp",EDGE,"E0.top"),sQuery(id+"F0.wireOp",EDGE,"E0.left"),sQuery(id+"F0.wireOp",EDGE,"E0.right")])],"isStart":false});
            var sketch = newSketch(context, id + "F14", { "sketchPlane" : qUnion([Q0])});
            skLineSegment(sketch, "E53", {"start": v(45, 0) * mm, "end": v(43.5, 1.5) * mm});
            skLineSegment(sketch, "E54", {"start": v(43.5, 1.5) * mm, "end": v(39.5, 1.5) * mm});
            skLineSegment(sketch, "E55", {"start": v(39.5, 1.5) * mm, "end": v(38, 0) * mm});
            skSolve(sketch);
        }
        {
            var Q0;
            {var subQ0=sQuery(id+"F14.wireOp",EDGE,"E53");Q0=makeQuery(id+"F14.imprint","IMPRINT",FACE,{"disambiguationData":[TD([[makeQuery(id+"F14.imprint","IMPRINT",EDGE,{"derivedFrom":subQ0}),1.0]])]});}
            extrude(context, id + "F15", {"entities" : qUnion([Q0]), "operationType" : NewBodyOperationType.ADD, "oppositeDirection" : true, "depth" : 5 * mm, "offsetDistance" : 25 * mm});
        }
        {
            var Q0;
            {var subQ0=sQuery(id+"F4.wireOp",EDGE,"E5");var subQ1=sQuery(id+"F4.wireOp",EDGE,"E4");Q0=makeQuery(id+"F7.boolean.opBoolean","SPLIT",EDGE,{"disambiguationData":[TD([makeQuery(id+"F7.opExtrude","SWEPT_FACE",FACE,{"disambiguationData":[OSD([sQuery(id+"F6.wireOp",EDGE,"E13.MirrorCS")])]})])],"derivedFrom":makeQuery(id+"F5.opExtrude","SWEPT_EDGE",EDGE,{"disambiguationData":[OSD([subQ1,subQ0])]})});}
            var Q1;
            {var subQ4=sQuery(id+"F0.wireOp",EDGE,"E0.bottom");var subQ5=sQuery(id+"F4.wireOp",EDGE,"E5");var subQ6=sQuery(id+"F4.wireOp",EDGE,"E4");Q1=makeQuery(id+"F7.boolean.opBoolean","SPLIT",EDGE,{"disambiguationData":[TD([makeQuery(id+"F1.opExtrude","SWEPT_FACE",FACE,{"disambiguationData":[OSD([subQ4])]})])],"derivedFrom":makeQuery(id+"F5.opExtrude","SWEPT_EDGE",EDGE,{"disambiguationData":[OSD([subQ6,subQ5])]})});}
            var Q2;
            {var subQ2=sQuery(id+"F0.wireOp",EDGE,"E0.top");var subQ4=sQuery(id+"F4.wireOp",EDGE,"E5");var subQ5=sQuery(id+"F4.wireOp",EDGE,"E4");Q2=makeQuery(id+"F7.boolean.opBoolean","SPLIT",EDGE,{"disambiguationData":[TD([makeQuery(id+"F1.opExtrude","SWEPT_FACE",FACE,{"disambiguationData":[OSD([subQ2])]})])],"derivedFrom":makeQuery(id+"F5.opExtrude","SWEPT_EDGE",EDGE,{"disambiguationData":[OSD([subQ5,subQ4])]})});}
            chamfer(context, id + "F16", {"entities" : qUnion([Q0, Q1, Q2]), "width" : 0.5 * mm, "tangentPropagation" : true});
        }
    });
